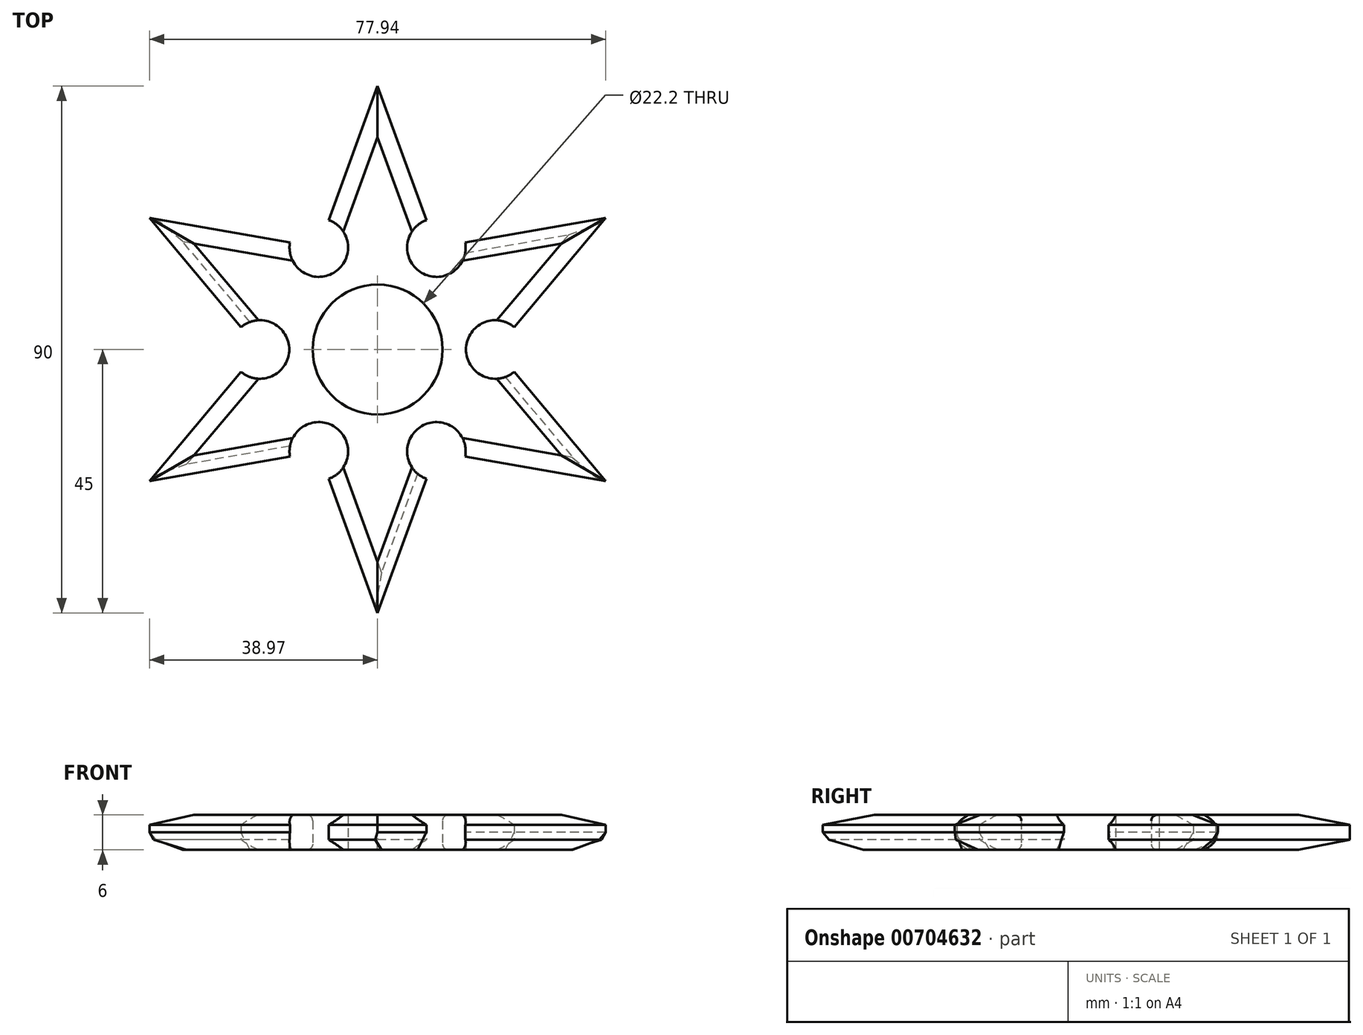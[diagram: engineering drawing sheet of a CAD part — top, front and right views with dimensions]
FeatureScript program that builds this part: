
annotation { "Feature Type Name" : "Feature", "Feature Type Description" : "" }
export const myFeature = defineFeature(function(context is Context, id is Id, definition is map)
    precondition{}
    {
        {
            var Q0;
            Q0=qCreatedBy(makeId("Top.planeOp"),FACE);
            var sketch = newSketch(context, id + "F0", { "sketchPlane" : qUnion([Q0])});
            skCircle(sketch, "E0", {"center": v(0, 0) * mm, "radius": 11.1 * mm});
            skLineSegment(sketch, "E1", {"start": v(0, 45) * mm, "end": v(-8.34, 22.1) * mm});
            skLineSegment(sketch, "E2.MirrorCS", {"start": v(0, 45) * mm, "end": v(8.34, 22.1) * mm});
            skLineSegment(sketch, "E3.1.0", {"start": v(-38.97, 22.5) * mm, "end": v(-14.97, 18.27) * mm});
            skLineSegment(sketch, "E3.1.1", {"start": v(-38.97, 22.5) * mm, "end": v(-23.31, 3.83) * mm});
            skLineSegment(sketch, "E3.2.0", {"start": v(-38.97, -22.5) * mm, "end": v(-23.31, -3.83) * mm});
            skLineSegment(sketch, "E3.2.1", {"start": v(-38.97, -22.5) * mm, "end": v(-14.97, -18.27) * mm});
            skLineSegment(sketch, "E3.3.0", {"start": v(0, -45) * mm, "end": v(-8.34, -22.1) * mm});
            skLineSegment(sketch, "E3.3.1", {"start": v(0, -45) * mm, "end": v(8.34, -22.1) * mm});
            skLineSegment(sketch, "E3.4.0", {"start": v(38.97, -22.5) * mm, "end": v(14.97, -18.27) * mm});
            skLineSegment(sketch, "E3.4.1", {"start": v(38.97, -22.5) * mm, "end": v(23.31, -3.83) * mm});
            skLineSegment(sketch, "E3.5.0", {"start": v(38.97, 22.5) * mm, "end": v(23.31, 3.83) * mm});
            skLineSegment(sketch, "E3.5.1", {"start": v(38.97, 22.5) * mm, "end": v(14.97, 18.27) * mm});
            skArc(sketch, "E4", {"start": v(-14.97, 18.27) * mm, "mid": v(-7.55, 13.08) * mm, "end": v(-8.34, 22.1) * mm});
            skArc(sketch, "E5.1.0", {"start": v(-23.31, -3.83) * mm, "mid": v(-15.1, 0) * mm, "end": v(-23.31, 3.83) * mm});
            skArc(sketch, "E5.2.0", {"start": v(-8.34, -22.1) * mm, "mid": v(-7.55, -13.08) * mm, "end": v(-14.97, -18.27) * mm});
            skArc(sketch, "E5.3.0", {"start": v(14.97, -18.27) * mm, "mid": v(7.55, -13.08) * mm, "end": v(8.34, -22.1) * mm});
            skArc(sketch, "E5.4.0", {"start": v(23.31, 3.83) * mm, "mid": v(15.1, 0) * mm, "end": v(23.31, -3.83) * mm});
            skArc(sketch, "E5.5.0", {"start": v(8.34, 22.1) * mm, "mid": v(7.55, 13.08) * mm, "end": v(14.97, 18.27) * mm});
            skSolve(sketch);
        }
        {
            var Q0;
            Q0=makeQuery(id+"F0.imprint","IMPRINT",FACE,{"disambiguationData":[TD([[makeQuery(id+"F0.imprint","IMPRINT",EDGE,{"derivedFrom":sQuery(id+"F0.wireOp",EDGE,"E0")}),-1.0]])]});
            extrude(context, id + "F1", {"entities" : qUnion([Q0]), "depth" : 6 * mm, "offsetDistance" : 25 * mm});
        }
        {
            var Q0;
            Q0=makeQuery(id+"F1.opExtrude","CAP_EDGE",EDGE,{"disambiguationData":[OSD([sQuery(id+"F0.wireOp",EDGE,"E1")])],"isStart":false});
            var Q1;
            Q1=makeQuery(id+"F1.opExtrude","CAP_EDGE",EDGE,{"disambiguationData":[OSD([sQuery(id+"F0.wireOp",EDGE,"E2.MirrorCS")])],"isStart":false});
            var Q2;
            Q2=makeQuery(id+"F1.opExtrude","CAP_EDGE",EDGE,{"disambiguationData":[OSD([sQuery(id+"F0.wireOp",EDGE,"E3.5.1")])],"isStart":false});
            var Q3;
            Q3=makeQuery(id+"F1.opExtrude","CAP_EDGE",EDGE,{"disambiguationData":[OSD([sQuery(id+"F0.wireOp",EDGE,"E3.5.0")])],"isStart":false});
            var Q4;
            Q4=makeQuery(id+"F1.opExtrude","CAP_EDGE",EDGE,{"disambiguationData":[OSD([sQuery(id+"F0.wireOp",EDGE,"E3.4.1")])],"isStart":false});
            var Q5;
            Q5=makeQuery(id+"F1.opExtrude","CAP_EDGE",EDGE,{"disambiguationData":[OSD([sQuery(id+"F0.wireOp",EDGE,"E3.4.0")])],"isStart":false});
            var Q6;
            Q6=makeQuery(id+"F1.opExtrude","CAP_EDGE",EDGE,{"disambiguationData":[OSD([sQuery(id+"F0.wireOp",EDGE,"E3.3.1")])],"isStart":false});
            var Q7;
            Q7=makeQuery(id+"F1.opExtrude","CAP_EDGE",EDGE,{"disambiguationData":[OSD([sQuery(id+"F0.wireOp",EDGE,"E3.3.0")])],"isStart":false});
            var Q8;
            Q8=makeQuery(id+"F1.opExtrude","CAP_EDGE",EDGE,{"disambiguationData":[OSD([sQuery(id+"F0.wireOp",EDGE,"E3.2.1")])],"isStart":false});
            var Q9;
            Q9=makeQuery(id+"F1.opExtrude","CAP_EDGE",EDGE,{"disambiguationData":[OSD([sQuery(id+"F0.wireOp",EDGE,"E3.2.0")])],"isStart":false});
            var Q10;
            Q10=makeQuery(id+"F1.opExtrude","CAP_EDGE",EDGE,{"disambiguationData":[OSD([sQuery(id+"F0.wireOp",EDGE,"E3.1.1")])],"isStart":false});
            var Q11;
            Q11=makeQuery(id+"F1.opExtrude","CAP_EDGE",EDGE,{"disambiguationData":[OSD([sQuery(id+"F0.wireOp",EDGE,"E3.1.0")])],"isStart":false});
            var Q12;
            Q12=makeQuery(id+"F1.opExtrude","CAP_EDGE",EDGE,{"disambiguationData":[OSD([sQuery(id+"F0.wireOp",EDGE,"E3.3.1")])],"isStart":true});
            var Q13;
            Q13=makeQuery(id+"F1.opExtrude","CAP_EDGE",EDGE,{"disambiguationData":[OSD([sQuery(id+"F0.wireOp",EDGE,"E3.3.0")])],"isStart":true});
            var Q14;
            Q14=makeQuery(id+"F1.opExtrude","CAP_EDGE",EDGE,{"disambiguationData":[OSD([sQuery(id+"F0.wireOp",EDGE,"E3.2.1")])],"isStart":true});
            var Q15;
            Q15=makeQuery(id+"F1.opExtrude","CAP_EDGE",EDGE,{"disambiguationData":[OSD([sQuery(id+"F0.wireOp",EDGE,"E3.2.0")])],"isStart":true});
            var Q16;
            Q16=makeQuery(id+"F1.opExtrude","CAP_EDGE",EDGE,{"disambiguationData":[OSD([sQuery(id+"F0.wireOp",EDGE,"E3.1.1")])],"isStart":true});
            var Q17;
            Q17=makeQuery(id+"F1.opExtrude","CAP_EDGE",EDGE,{"disambiguationData":[OSD([sQuery(id+"F0.wireOp",EDGE,"E3.1.0")])],"isStart":true});
            var Q18;
            Q18=makeQuery(id+"F1.opExtrude","CAP_EDGE",EDGE,{"disambiguationData":[OSD([sQuery(id+"F0.wireOp",EDGE,"E1")])],"isStart":true});
            var Q19;
            Q19=makeQuery(id+"F1.opExtrude","CAP_EDGE",EDGE,{"disambiguationData":[OSD([sQuery(id+"F0.wireOp",EDGE,"E2.MirrorCS")])],"isStart":true});
            var Q20;
            Q20=makeQuery(id+"F1.opExtrude","CAP_EDGE",EDGE,{"disambiguationData":[OSD([sQuery(id+"F0.wireOp",EDGE,"E3.5.1")])],"isStart":true});
            var Q21;
            Q21=makeQuery(id+"F1.opExtrude","CAP_EDGE",EDGE,{"disambiguationData":[OSD([sQuery(id+"F0.wireOp",EDGE,"E3.5.0")])],"isStart":true});
            var Q22;
            Q22=makeQuery(id+"F1.opExtrude","CAP_EDGE",EDGE,{"disambiguationData":[OSD([sQuery(id+"F0.wireOp",EDGE,"E3.4.1")])],"isStart":true});
            var Q23;
            Q23=makeQuery(id+"F1.opExtrude","CAP_EDGE",EDGE,{"disambiguationData":[OSD([sQuery(id+"F0.wireOp",EDGE,"E3.4.0")])],"isStart":true});
            chamfer(context, id + "F2", {"entities" : qUnion([Q0, Q1, Q2, Q3, Q4, Q5, Q6, Q7, Q8, Q9, Q10, Q11, Q12, Q13, Q14, Q15, Q16, Q17, Q18, Q19, Q20, Q21, Q22, Q23]), "chamferType" : ChamferType.OFFSET_ANGLE, "width" : 3 * mm, "oppositeDirection" : false, "angle" : 30 * degree, "tangentPropagation" : true});
        }
        {
            var Q0;
            Q0=makeQuery(id+"F1.opExtrude","CAP_EDGE",EDGE,{"disambiguationData":[OSD([sQuery(id+"F0.wireOp",EDGE,"E0")])],"isStart":true});
            var Q1;
            Q1=makeQuery(id+"F1.opExtrude","CAP_EDGE",EDGE,{"disambiguationData":[OSD([sQuery(id+"F0.wireOp",EDGE,"E0")])],"isStart":false});
            fillet(context, id + "F3", {"entities" : qUnion([Q0, Q1]), "radius" : 1 * mm, "tangentPropagation" : true, "allowEdgeOverflow" : false});
        }
    });
